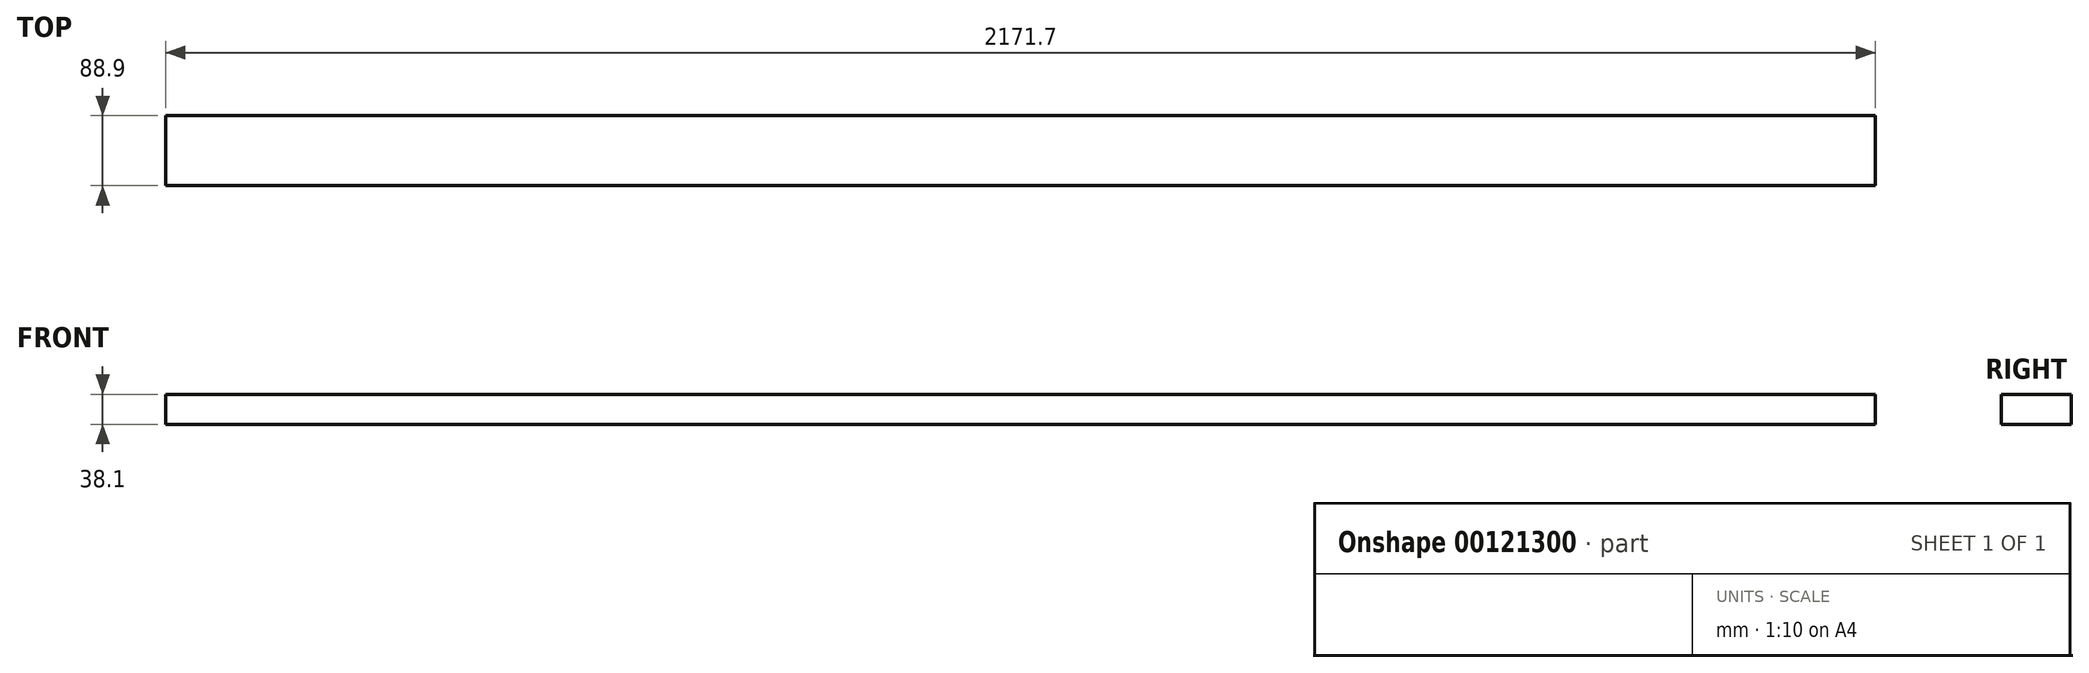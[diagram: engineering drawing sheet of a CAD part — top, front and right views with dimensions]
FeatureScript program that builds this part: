
annotation { "Feature Type Name" : "Feature", "Feature Type Description" : "" }
export const myFeature = defineFeature(function(context is Context, id is Id, definition is map)
    precondition{}
    {
        {
            var Q0;
            Q0=qCreatedBy(makeId("Front.planeOp"),FACE);
            var sketch = newSketch(context, id + "F0", { "sketchPlane" : qUnion([Q0])});
            skLineSegment(sketch, "E0.bottom", {"start": v(0, 0) * mm, "end": v(2171.7, 0) * mm});
            skLineSegment(sketch, "E0.top", {"start": v(0, 38.1) * mm, "end": v(2171.7, 38.1) * mm});
            skLineSegment(sketch, "E0.left", {"start": v(0, 0) * mm, "end": v(0, 38.1) * mm});
            skLineSegment(sketch, "E0.right", {"start": v(2171.7, 0) * mm, "end": v(2171.7, 38.1) * mm});
            skSolve(sketch);
        }
        {
            var Q0;
            Q0=makeQuery(id+"F0.imprint","IMPRINT",FACE,{"disambiguationData":[TD([[makeQuery(id+"F0.imprint","IMPRINT",EDGE,{"derivedFrom":sQuery(id+"F0.wireOp",EDGE,"E0.bottom")}),1.0]])]});
            extrude(context, id + "F1", {"entities" : qUnion([Q0]), "depth" : 88.9 * mm});
        }
    });
